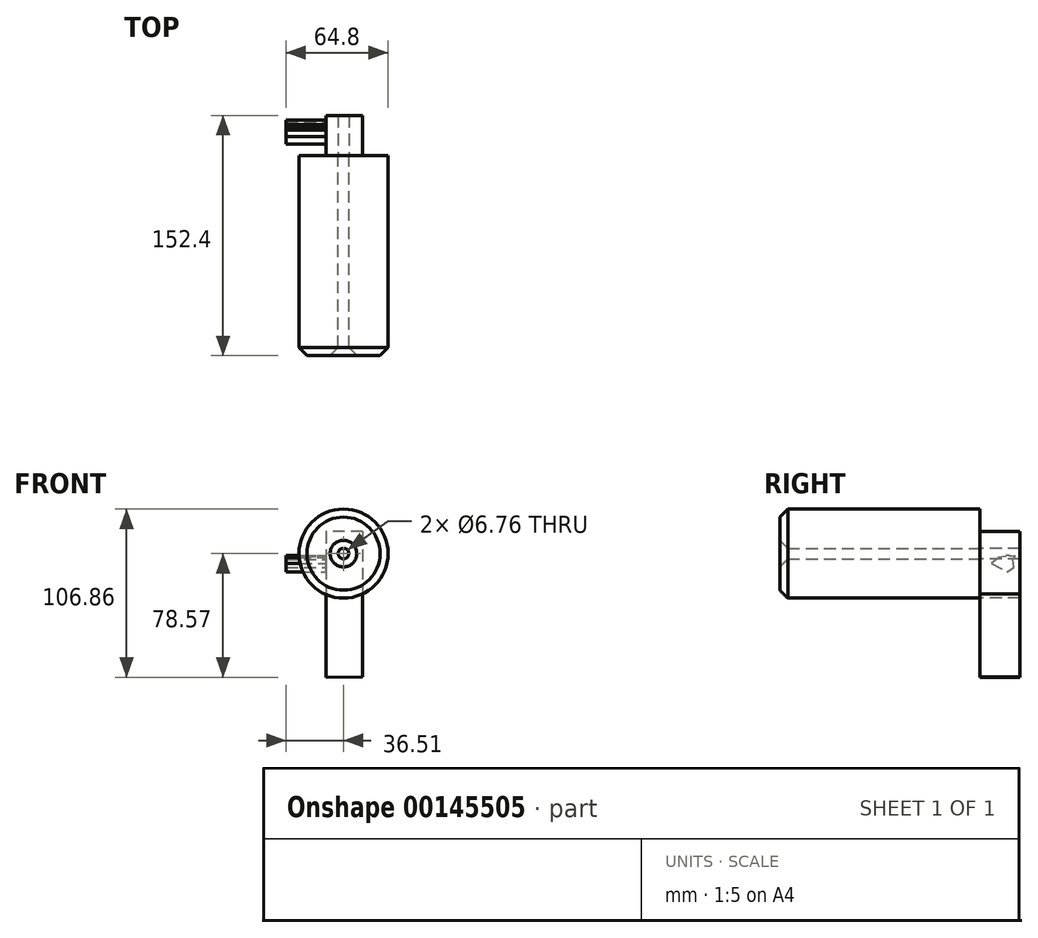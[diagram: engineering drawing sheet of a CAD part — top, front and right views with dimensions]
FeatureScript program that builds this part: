
annotation { "Feature Type Name" : "Feature", "Feature Type Description" : "" }
export const myFeature = defineFeature(function(context is Context, id is Id, definition is map)
    precondition{}
    {
        {
            var Q0;
            Q0=qCreatedBy(makeId("Front.planeOp"),FACE);
            var sketch = newSketch(context, id + "F0", { "sketchPlane" : qUnion([Q0])});
            skCircle(sketch, "E0", {"center": v(0, 0) * mm, "radius": 28.3 * mm});
            skCircle(sketch, "E1", {"center": v(0, 0) * mm, "radius": 3.38 * mm});
            skSolve(sketch);
        }
        {
            var Q0;
            Q0=makeQuery(id+"F0.imprint","IMPRINT",FACE,{"disambiguationData":[TD([[makeQuery(id+"F0.imprint","IMPRINT",EDGE,{"derivedFrom":sQuery(id+"F0.wireOp",EDGE,"E0")}),1.0]])]});
            extrude(context, id + "F1", {"entities" : qUnion([Q0]), "depth" : 127 * mm});
        }
        {
            var Q0;
            Q0=makeQuery(id+"F1.opExtrude","CAP_FACE",FACE,{"disambiguationData":[OSD([sQuery(id+"F0.wireOp",EDGE,"E0"),sQuery(id+"F0.wireOp",EDGE,"E1")])],"isStart":true});
            var sketch = newSketch(context, id + "F2", { "sketchPlane" : qUnion([Q0])});
            skLineSegment(sketch, "E2", {"start": v(-12.22, 14.02) * mm, "end": v(11.11, 14.02) * mm});
            skLineSegment(sketch, "E3", {"start": v(11.11, 14.02) * mm, "end": v(11.11, -78.57) * mm});
            skLineSegment(sketch, "E4", {"start": v(-12.22, 14.02) * mm, "end": v(-12.22, -78.36) * mm});
            skLineSegment(sketch, "E5", {"start": v(-12.22, -78.36) * mm, "end": v(11.11, -78.57) * mm});
            skSolve(sketch);
        }
        {
            var Q0;
            {var subQ0=sQuery(id+"F2.wireOp",EDGE,"E5");Q0=makeQuery(id+"F2.imprint","IMPRINT",FACE,{"disambiguationData":[TD([[makeQuery(id+"F2.imprint","IMPRINT",EDGE,{"derivedFrom":subQ0}),1.0]])]});}
            extrude(context, id + "F3", {"entities" : qUnion([Q0]), "depth" : 25.4 * mm});
        }
        {
            var Q0;
            {var subQ1=sQuery(id+"F2.wireOp",EDGE,"E2");Q0=makeQuery(id+"F2.imprint","IMPRINT",FACE,{"disambiguationData":[TD([[makeQuery(id+"F2.imprint","IMPRINT",EDGE,{"derivedFrom":subQ1}),-1.0]])]});}
            extrude(context, id + "F4", {"entities" : qUnion([Q0]), "depth" : 25.4 * mm});
        }
        {
            var Q0;
            Q0=makeQuery(id+"F1.opExtrude","CAP_EDGE",EDGE,{"disambiguationData":[OSD([sQuery(id+"F0.wireOp",EDGE,"E1")])],"isStart":false});
            var Q1;
            Q1=makeQuery(id+"F1.opExtrude","CAP_EDGE",EDGE,{"disambiguationData":[OSD([sQuery(id+"F0.wireOp",EDGE,"E0")])],"isStart":false});
            chamfer(context, id + "F5", {"entities" : qUnion([Q0, Q1]), "width" : 5.08 * mm, "tangentPropagation" : true});
        }
        {
            var Q0;
            Q0=makeQuery(id+"F4.opExtrude","SWEPT_FACE",FACE,{"disambiguationData":[OSD([sQuery(id+"F2.wireOp",EDGE,"E3")])]});
            var sketch = newSketch(context, id + "F6", { "sketchPlane" : qUnion([Q0])});
            skLineSegment(sketch, "E6", {"start": v(-19.82, -1.8) * mm, "end": v(-19.33, -1.38) * mm});
            skLineSegment(sketch, "E7", {"start": v(-19.33, -1.38) * mm, "end": v(-18.96, -1.38) * mm});
            skLineSegment(sketch, "E8", {"start": v(-18.96, -1.38) * mm, "end": v(-18.56, -1.1) * mm});
            skLineSegment(sketch, "E9", {"start": v(-18.56, -1.1) * mm, "end": v(-17.91, -1.1) * mm});
            skLineSegment(sketch, "E10", {"start": v(-17.91, -1.1) * mm, "end": v(-16.96, -1.1) * mm});
            skLineSegment(sketch, "E11", {"start": v(-16.96, -1.1) * mm, "end": v(-16.25, -1.9) * mm});
            skLineSegment(sketch, "E12", {"start": v(-16.25, -1.9) * mm, "end": v(-12.17, -2.49) * mm});
            skLineSegment(sketch, "E13", {"start": v(-12.17, -2.49) * mm, "end": v(-7.4, -6.2) * mm});
            skLineSegment(sketch, "E14", {"start": v(-7.4, -6.2) * mm, "end": v(-17.11, -11.52) * mm});
            skLineSegment(sketch, "E15", {"start": v(-17.11, -11.52) * mm, "end": v(-21.72, -8.66) * mm});
            skLineSegment(sketch, "E16", {"start": v(-21.72, -8.66) * mm, "end": v(-21.1, -3.75) * mm});
            skLineSegment(sketch, "E17", {"start": v(-21.1, -3.75) * mm, "end": v(-22.64, -1.63) * mm});
            skLineSegment(sketch, "E18", {"start": v(-22.64, -1.63) * mm, "end": v(-19.82, -1.8) * mm});
            skSolve(sketch);
        }
        {
            var Q0;
            Q0=makeQuery(id+"F6.imprint","IMPRINT",FACE,{"disambiguationData":[TD([[makeQuery(id+"F6.imprint","IMPRINT",EDGE,{"derivedFrom":sQuery(id+"F6.wireOp",EDGE,"E6")}),-1.0]])]});
            extrude(context, id + "F7", {"entities" : qUnion([Q0]), "operationType" : NewBodyOperationType.ADD, "depth" : 25.4 * mm});
        }
    });
